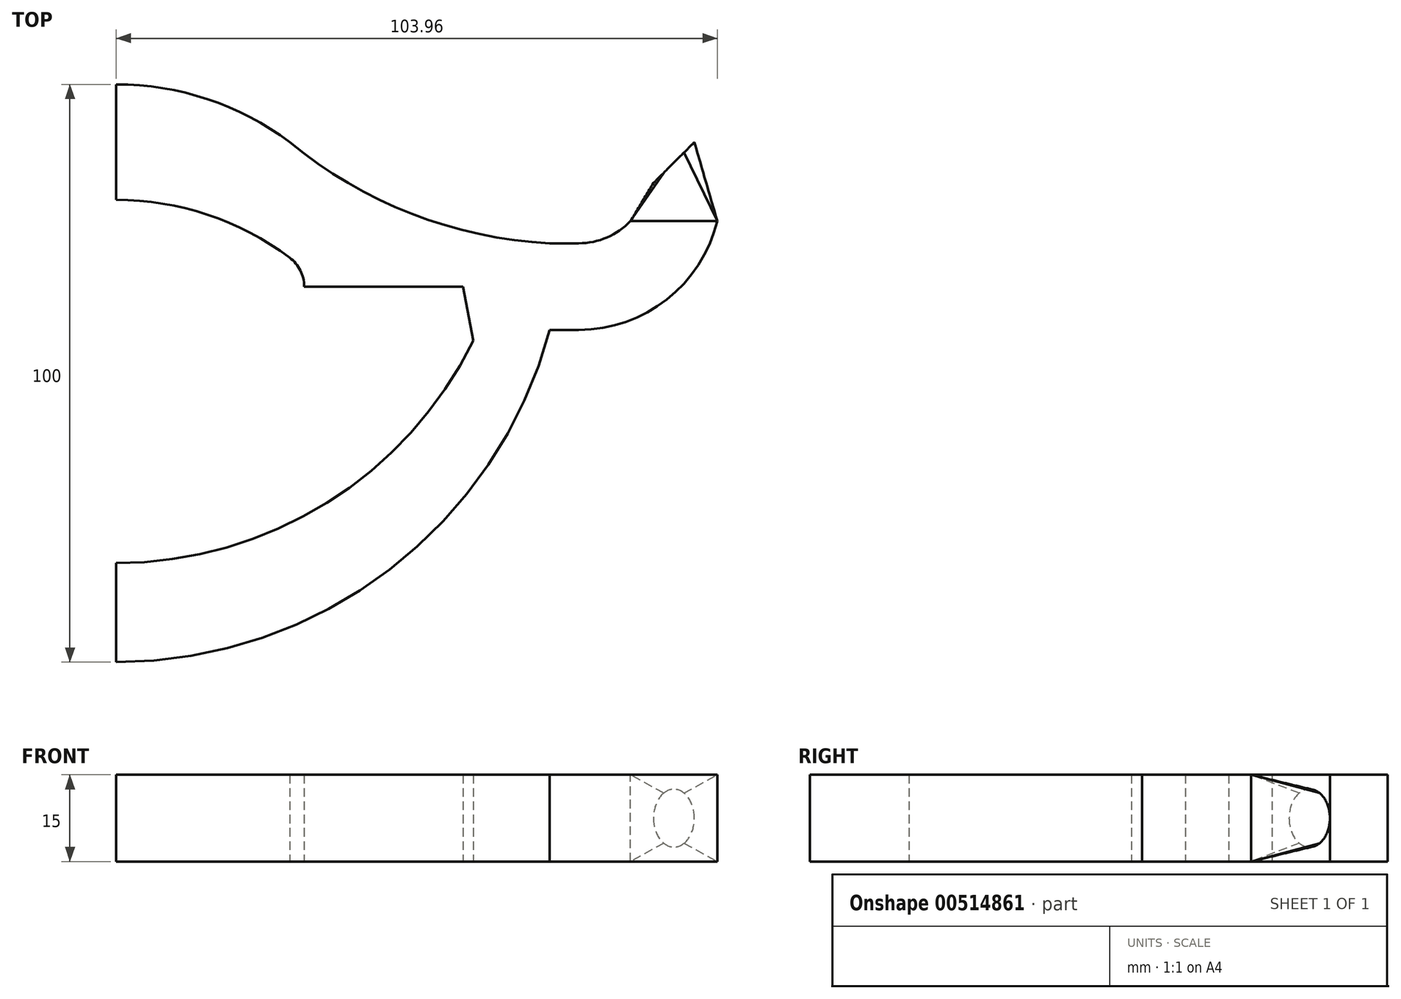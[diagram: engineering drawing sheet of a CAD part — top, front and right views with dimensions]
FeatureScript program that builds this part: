
annotation { "Feature Type Name" : "Feature", "Feature Type Description" : "" }
export const myFeature = defineFeature(function(context is Context, id is Id, definition is map)
    precondition{}
    {
        {
            var Q0;
            Q0=qCreatedBy(makeId("Top.planeOp"),FACE);
            var sketch = newSketch(context, id + "F0", { "sketchPlane" : qUnion([Q0])});
            skLineSegment(sketch, "E0.left", {"start": v(-50, 50) * mm, "end": v(-50, -50) * mm});
            skPoint(sketch, "E0.middle", {"position": v(0, 0) * mm});
            skLineSegment(sketch, "E1", {"start": v(-50, 50) * mm, "end": v(-50, 40) * mm});
            skLineSegment(sketch, "E2", {"start": v(50, 40) * mm, "end": v(42.93, 32.93) * mm});
            skLineSegment(sketch, "E3", {"start": v(42.93, 32.93) * mm, "end": v(46.46, 36.46) * mm});
            skLineSegment(sketch, "E4", {"start": v(-50, 0) * mm, "end": v(-50, -10) * mm});
            skLineSegment(sketch, "E5", {"start": v(-50, -10) * mm, "end": v(-50, 15) * mm});
            skLineSegment(sketch, "E6", {"start": v(-50, 15) * mm, "end": v(114.78, 15) * mm});
            skLineSegment(sketch, "E7", {"start": v(42.93, 32.93) * mm, "end": v(42.93, -37.04) * mm});
            skLineSegment(sketch, "E8", {"start": v(-50, 15) * mm, "end": v(30, 15) * mm});
            skLineSegment(sketch, "E9", {"start": v(30, 15) * mm, "end": v(30, 30) * mm});
            skLineSegment(sketch, "E10", {"start": v(30, 15) * mm, "end": v(30, 0) * mm});
            skLineSegment(sketch, "E11", {"start": v(42.93, 32.93) * mm, "end": v(81, 32.93) * mm});
            skLineSegment(sketch, "E12", {"start": v(46.46, 36.46) * mm, "end": v(46.46, 32.93) * mm});
            skLineSegment(sketch, "E13", {"start": v(46.46, 36.46) * mm, "end": v(46.46, 0) * mm});
            skLineSegment(sketch, "E14", {"start": v(46.46, 36.46) * mm, "end": v(62.14, 20.79) * mm});
            skLineSegment(sketch, "E15", {"start": v(-50, 50) * mm, "end": v(-109.66, 50) * mm});
            skLineSegment(sketch, "E16", {"start": v(-50, 40) * mm, "end": v(-110.5, 40) * mm});
            skLineSegment(sketch, "E17", {"start": v(-50, 15) * mm, "end": v(-113.83, 15) * mm});
            skLineSegment(sketch, "E18", {"start": v(-50, 0) * mm, "end": v(-113, 0) * mm});
            skLineSegment(sketch, "E19", {"start": v(-50, -10) * mm, "end": v(-113, -10) * mm});
            skLineSegment(sketch, "E20", {"start": v(-50, -50) * mm, "end": v(-111.33, -50) * mm});
            skLineSegment(sketch, "E21", {"start": v(30, 30) * mm, "end": v(95.7, 30) * mm});
            skPoint(sketch, "E22", {"position": v(42.93, 30) * mm});
            skPoint(sketch, "E23", {"position": v(46.46, 30) * mm});
            skPoint(sketch, "E24", {"position": v(42.93, 26.34) * mm});
            skLineSegment(sketch, "E25", {"start": v(30, 15) * mm, "end": v(30, 7.5) * mm});
            skLineSegment(sketch, "E26", {"start": v(30, 15) * mm, "end": v(30, 22.5) * mm});
            skLineSegment(sketch, "E27", {"start": v(30, 15) * mm, "end": v(0, 15) * mm});
            skLineSegment(sketch, "E28", {"start": v(-50, 15) * mm, "end": v(-30, 15) * mm});
            skLineSegment(sketch, "E29", {"start": v(-30, 15) * mm, "end": v(-10, 15) * mm});
            skLineSegment(sketch, "E30", {"start": v(-10, 15) * mm, "end": v(10, 15) * mm});
            skSolve(sketch);
        }
        {
            var Q0;
            Q0=sQuery(id+"F0.wireOp",EDGE,"E2");
            cPlane(context, id + "F1", {"entities" : qUnion([Q0]), "cplaneType" : CPlaneType.LINE_ANGLE, "offset" : 25 * mm, "angle" : 90 * degree, "width" : 150 * mm, "height" : 150 * mm});
        }
        {
            var Q0;
            Q0=qCreatedBy(id+"F1.planeOp",FACE);
            var sketch = newSketch(context, id + "F2", { "sketchPlane" : qUnion([Q0])});
            skCircle(sketch, "E31", {"center": v(58.64, 0) * mm, "radius": 5 * mm});
            skSolve(sketch);
        }
        {
            var Q0;
            Q0=sQuery(id+"F0.wireOp",VERTEX,"E6.start");
            var Q1;
            Q1=qCreatedBy(makeId("Right.planeOp"),FACE);
            cPlane(context, id + "F3", {"entities" : qUnion([Q0, Q1]), "cplaneType" : CPlaneType.PLANE_POINT, "offset" : 25 * mm, "width" : 150 * mm, "height" : 150 * mm});
        }
        {
            var Q0;
            Q0=qCreatedBy(id+"F3.planeOp",FACE);
            var sketch = newSketch(context, id + "F4", { "sketchPlane" : qUnion([Q0])});
            skPoint(sketch, "E32", {"position": v(15, 0) * mm});
            skLineSegment(sketch, "E33", {"start": v(50, 10) * mm, "end": v(-20, 10) * mm});
            skLineSegment(sketch, "E34", {"start": v(50, -10) * mm, "end": v(-20, -10) * mm});
            skLineSegment(sketch, "E35", {"start": v(50, 10) * mm, "end": v(50, -10) * mm});
            skLineSegment(sketch, "E36", {"start": v(-20, 10) * mm, "end": v(-20, -10) * mm});
            skLineSegment(sketch, "E37", {"start": v(-49.86, 0) * mm, "end": v(-49.86, 10) * mm});
            skLineSegment(sketch, "E38", {"start": v(-49.86, 0) * mm, "end": v(-49.86, -10) * mm});
            skLineSegment(sketch, "E39", {"start": v(-49.86, 10) * mm, "end": v(-32.86, 10) * mm});
            skLineSegment(sketch, "E40", {"start": v(-32.86, 10) * mm, "end": v(-32.86, -10) * mm});
            skLineSegment(sketch, "E41", {"start": v(-32.86, -10) * mm, "end": v(-49.86, -10) * mm});
            skPoint(sketch, "E42", {"position": v(-32.86, 0) * mm});
            skSolve(sketch);
        }
        {
            var Q0;
            Q0=sQuery(id+"F0.wireOp",VERTEX,"E9.start");
            var Q1;
            Q1=qCreatedBy(id+"F3.planeOp",FACE);
            var Q2;
            Q2=qBodyType(qCreatedBy(id+"FoWz66eWp3AvkS4_1",EDGE),BodyType.WIRE);
            cPlane(context, id + "F5", {"entities" : qUnion([Q0, Q1, Q2]), "cplaneType" : CPlaneType.PLANE_POINT, "offset" : 25 * mm, "width" : 150 * mm, "height" : 150 * mm});
        }
        {
            var Q0;
            Q0=qCreatedBy(id+"F5.planeOp",FACE);
            var sketch = newSketch(context, id + "F6", { "sketchPlane" : qUnion([Q0])});
            skLineSegment(sketch, "E43", {"start": v(22.5, 7.5) * mm, "end": v(7.5, 7.5) * mm});
            skLineSegment(sketch, "E44", {"start": v(22.5, -7.5) * mm, "end": v(7.5, -7.5) * mm});
            skLineSegment(sketch, "E45", {"start": v(22.5, 7.5) * mm, "end": v(22.5, -7.5) * mm});
            skLineSegment(sketch, "E46", {"start": v(7.5, 7.5) * mm, "end": v(7.5, -7.5) * mm});
            skSolve(sketch);
        }
        {
            var Q0;
            Q0=qCreatedBy(makeId("Front.planeOp"),FACE);
            var Q1;
            Q1=sQuery(id+"F0.wireOp",VERTEX,"E24");
            cPlane(context, id + "F7", {"entities" : qUnion([Q0, Q1]), "cplaneType" : CPlaneType.PLANE_POINT, "offset" : 25 * mm, "width" : 150 * mm, "height" : 150 * mm});
        }
        {
            var Q0;
            Q0=qCreatedBy(id+"F7.planeOp",FACE);
            var sketch = newSketch(context, id + "F8", { "sketchPlane" : qUnion([Q0])});
            skPoint(sketch, "E47", {"position": v(46.46, 0) * mm});
            skLineSegment(sketch, "E48", {"start": v(38.96, 0) * mm, "end": v(38.96, -7.5) * mm});
            skLineSegment(sketch, "E49", {"start": v(38.96, 0) * mm, "end": v(38.96, 7.5) * mm});
            skLineSegment(sketch, "E50", {"start": v(53.96, 0) * mm, "end": v(53.96, -7.5) * mm});
            skLineSegment(sketch, "E51", {"start": v(53.96, 0) * mm, "end": v(53.96, 7.5) * mm});
            skLineSegment(sketch, "E52", {"start": v(38.96, -7.5) * mm, "end": v(53.96, -7.5) * mm});
            skLineSegment(sketch, "E53", {"start": v(38.96, 7.5) * mm, "end": v(53.96, 7.5) * mm});
            skSolve(sketch);
        }
        {
            var Q0;
            Q0=makeQuery(id+"F2.imprint","IMPRINT",FACE,{"disambiguationData":[TD([[makeQuery(id+"F2.imprint","IMPRINT",EDGE,{"derivedFrom":sQuery(id+"F2.wireOp",EDGE,"E31")}),1.0]])]});
            var Q1;
            Q1=makeQuery(id+"F8.imprint","IMPRINT",FACE,{"disambiguationData":[TD([[makeQuery(id+"F8.imprint","IMPRINT",EDGE,{"derivedFrom":sQuery(id+"F8.wireOp",EDGE,"E48")}),1.0]])]});
            loft(context, id + "F9", {"sheetProfilesArray" : [{ "sheetProfileEntities" : qUnion([Q0]) }, { "sheetProfileEntities" : qUnion([Q1]) }]});
        }
        {
            var Q0;
            Q0=sQuery(id+"F0.wireOp",VERTEX,"E17.start");
            var Q1;
            Q1=qCreatedBy(makeId("Right.planeOp"),FACE);
            cPlane(context, id + "F10", {"entities" : qUnion([Q0, Q1]), "cplaneType" : CPlaneType.PLANE_POINT, "offset" : 25 * mm, "width" : 150 * mm, "height" : 150 * mm});
        }
        {
            var Q0;
            Q0=sQuery(id+"F0.wireOp",VERTEX,"E30.end");
            var Q1;
            Q1=qCreatedBy(id+"F5.planeOp",FACE);
            cPlane(context, id + "F11", {"entities" : qUnion([Q0, Q1]), "cplaneType" : CPlaneType.PLANE_POINT, "offset" : 25 * mm, "width" : 150 * mm, "height" : 150 * mm});
        }
        {
            var Q0;
            Q0=qCreatedBy(id+"F11.planeOp",FACE);
            var sketch = newSketch(context, id + "F12", { "sketchPlane" : qUnion([Q0])});
            skPoint(sketch, "E54", {"position": v(15, 0) * mm});
            skLineSegment(sketch, "E55", {"start": v(30, -10) * mm, "end": v(30, 10) * mm});
            skLineSegment(sketch, "E56", {"start": v(0, 10) * mm, "end": v(0, -10) * mm});
            skLineSegment(sketch, "E57", {"start": v(30, 10) * mm, "end": v(0, 10) * mm});
            skLineSegment(sketch, "E58", {"start": v(30, -10) * mm, "end": v(0, -10) * mm});
            skSolve(sketch);
        }
        {
            var Q0;
            Q0=sQuery(id+"F0.wireOp",VERTEX,"E30.start");
            var Q1;
            Q1=qCreatedBy(makeId("Right.planeOp"),FACE);
            cPlane(context, id + "F13", {"entities" : qUnion([Q0, Q1]), "cplaneType" : CPlaneType.PLANE_POINT, "offset" : 25 * mm, "width" : 150 * mm, "height" : 150 * mm});
        }
        {
            var Q0;
            Q0=sQuery(id+"F0.wireOp",VERTEX,"E29.start");
            var Q1;
            Q1=qCreatedBy(id+"F13.planeOp",FACE);
            cPlane(context, id + "F14", {"entities" : qUnion([Q0, Q1]), "cplaneType" : CPlaneType.PLANE_POINT, "offset" : 25 * mm, "width" : 150 * mm, "height" : 150 * mm});
        }
        {
            var Q0;
            Q0=sQuery(id+"F8.wireOp",VERTEX,"E48.start");
            var Q1;
            Q1=qCreatedBy(makeId("Top.planeOp"),FACE);
            cPlane(context, id + "F15", {"entities" : qUnion([Q0, Q1]), "cplaneType" : CPlaneType.PLANE_POINT, "offset" : 25 * mm, "width" : 150 * mm, "height" : 150 * mm});
        }
        {
            var Q0;
            Q0=qCreatedBy(id+"F15.planeOp",FACE);
            var sketch = newSketch(context, id + "F16", { "sketchPlane" : qUnion([Q0])});
            skPoint(sketch, "E59", {"position": v(30, 22.5) * mm});
            skPoint(sketch, "E60", {"position": v(38.96, 26.34) * mm});
            skPoint(sketch, "E61", {"position": v(30, 7.5) * mm});
            skPoint(sketch, "E62", {"position": v(53.96, 26.34) * mm});
            skArc(sketch, "E63", {"start": v(30, 22.5) * mm, "mid": v(34.88, 23.5) * mm, "end": v(38.96, 26.34) * mm});
            skArc(sketch, "E64", {"start": v(30, 7.5) * mm, "mid": v(45.24, 12.77) * mm, "end": v(53.96, 26.34) * mm});
            skLineSegment(sketch, "E65", {"start": v(30, 22.5) * mm, "end": v(30, 7.5) * mm});
            skLineSegment(sketch, "E66", {"start": v(38.96, 26.34) * mm, "end": v(53.96, 26.34) * mm});
            skSolve(sketch);
        }
        {
            var Q0;
            Q0=makeQuery(id+"F16.imprint","IMPRINT",FACE,{"disambiguationData":[TD([[makeQuery(id+"F16.imprint","IMPRINT",EDGE,{"derivedFrom":sQuery(id+"F16.wireOp",EDGE,"E63")}),-1.0]])]});
            extrude(context, id + "F17", {"entities" : qUnion([Q0]), "operationType" : NewBodyOperationType.ADD, "endBound" : BoundingType.SYMMETRIC, "depth" : 15 * mm, "offsetDistance" : 25 * mm});
        }
        {
            var Q0;
            Q0=qCreatedBy(makeId("Top.planeOp"),FACE);
            var sketch = newSketch(context, id + "F18", { "sketchPlane" : qUnion([Q0])});
            skPoint(sketch, "E67", {"position": v(30, 22.5) * mm});
            skPoint(sketch, "E68", {"position": v(30, 7.5) * mm});
            skPoint(sketch, "E69", {"position": v(-50, 50) * mm});
            skPoint(sketch, "E70", {"position": v(-50, -20) * mm});
            skLineSegment(sketch, "E71", {"start": v(-50, 50) * mm, "end": v(-56.58, 50) * mm});
            skLineSegment(sketch, "E72", {"start": v(-50, -20) * mm, "end": v(-57.7, -20) * mm});
            skLineSegment(sketch, "E73", {"start": v(30, 22.5) * mm, "end": v(25, 22.5) * mm});
            skPoint(sketch, "E74", {"position": v(-50, 40) * mm});
            skPoint(sketch, "E75", {"position": v(-50, 15) * mm});
            skPoint(sketch, "E76", {"position": v(-50, 0) * mm});
            skPoint(sketch, "E77", {"position": v(-50, -10) * mm});
            skLineSegment(sketch, "E78.MirrorCS", {"start": v(30, 7.5) * mm, "end": v(25, 7.5) * mm});
            skLineSegment(sketch, "E79", {"start": v(-50, 50) * mm, "end": v(-50, -20) * mm});
            skLineSegment(sketch, "E80", {"start": v(30, 22.5) * mm, "end": v(30, 7.5) * mm});
            skLineSegment(sketch, "E81", {"start": v(25, 22.5) * mm, "end": v(25, 7.5) * mm});
            skPoint(sketch, "E82", {"position": v(25, 15) * mm});
            skLineSegment(sketch, "E83", {"start": v(25, 15) * mm, "end": v(-20, 15) * mm});
            skLineSegment(sketch, "E84", {"start": v(-50, 40) * mm, "end": v(-20, 40) * mm});
            skArc(sketch, "E85", {"start": v(-20, 40) * mm, "mid": v(-34.19, 47.43) * mm, "end": v(-50, 50) * mm});
            skLineSegment(sketch, "E86", {"start": v(-20, 40) * mm, "end": v(-14.1, 35.57) * mm});
            skArc(sketch, "E87", {"start": v(-20, 40) * mm, "mid": v(1.08, 27.6) * mm, "end": v(25, 22.5) * mm});
            skArc(sketch, "E88.MirrorCS", {"start": v(-20, -10) * mm, "mid": v(-34.19, -17.43) * mm, "end": v(-50, -20) * mm});
            skArc(sketch, "E89.MirrorCS", {"start": v(-20, -10) * mm, "mid": v(1.08, 2.4) * mm, "end": v(25, 7.5) * mm});
            skPoint(sketch, "E90", {"position": v(10, 15) * mm});
            skLineSegment(sketch, "E91", {"start": v(11.77, 5.67) * mm, "end": v(10, 15) * mm});
            skPoint(sketch, "E92", {"position": v(-50, -32.86) * mm});
            skPoint(sketch, "E93", {"position": v(-50, -50) * mm});
            skLineSegment(sketch, "E94", {"start": v(-50, -32.86) * mm, "end": v(-55.92, -32.86) * mm});
            skLineSegment(sketch, "E95", {"start": v(-50, -32.86) * mm, "end": v(-50, -42.86) * mm});
            skLineSegment(sketch, "E96", {"start": v(-50, -42.86) * mm, "end": v(-32.06, -42.86) * mm});
            skLineSegment(sketch, "E97", {"start": v(-50, -20) * mm, "end": v(-50, -24.93) * mm});
            skLineSegment(sketch, "E98", {"start": v(-50, -24.93) * mm, "end": v(-42.8, -24.93) * mm});
            skLineSegment(sketch, "E99", {"start": v(-50, -32.86) * mm, "end": v(-5.32, -32.86) * mm});
            skLineSegment(sketch, "E100", {"start": v(-20, -10) * mm, "end": v(-18.9, -9.1) * mm});
            skLineSegment(sketch, "E101", {"start": v(-50, -50) * mm, "end": v(-61.6, -50) * mm});
            skLineSegment(sketch, "E102", {"start": v(-20, -37.52) * mm, "end": v(-20, -61.03) * mm});
            skLineSegment(sketch, "E103", {"start": v(-50, -50) * mm, "end": v(-20, -50) * mm});
            skArc(sketch, "E104", {"start": v(-50, -32.86) * mm, "mid": v(-13.6, -22.43) * mm, "end": v(11.77, 5.67) * mm});
            skArc(sketch, "E105", {"start": v(-50, -50) * mm, "mid": v(-2.75, -33.97) * mm, "end": v(25, 7.5) * mm});
            skLineSegment(sketch, "E106", {"start": v(-50, -32.86) * mm, "end": v(-50, -50) * mm});
            skLineSegment(sketch, "E107", {"start": v(-50, 15) * mm, "end": v(-50, 24) * mm});
            skLineSegment(sketch, "E108", {"start": v(-50, 15) * mm, "end": v(-50, 6) * mm});
            skLineSegment(sketch, "E109", {"start": v(-50, -20) * mm, "end": v(-50, 5) * mm});
            skLineSegment(sketch, "E110", {"start": v(-50, 5) * mm, "end": v(-40.99, 5) * mm});
            skArc(sketch, "E111.MirrorCS", {"start": v(-20, 20) * mm, "mid": v(-34.19, 27.43) * mm, "end": v(-50, 30) * mm});
            skLineSegment(sketch, "E112", {"start": v(-50, 50) * mm, "end": v(-50, 25) * mm});
            skLineSegment(sketch, "E113", {"start": v(-50, 25) * mm, "end": v(-38.68, 25) * mm});
            skArc(sketch, "E114.MirrorCS", {"start": v(-20, 10) * mm, "mid": v(-34.19, 2.57) * mm, "end": v(-50, 0) * mm});
            skLineSegment(sketch, "E115", {"start": v(-20, 20) * mm, "end": v(-20, 10) * mm});
            skLineSegment(sketch, "E116", {"start": v(-20, 10) * mm, "end": v(-15.23, 13.58) * mm});
            skLineSegment(sketch, "E117", {"start": v(-20, 20) * mm, "end": v(-16.17, 17.13) * mm});
            skArc(sketch, "E118", {"start": v(-20, 10) * mm, "mid": v(-17.5, 15) * mm, "end": v(-20, 20) * mm});
            skSolve(sketch);
        }
        {
            var Q0;
            Q0=makeQuery(id+"F18.imprint","IMPRINT",FACE,{"disambiguationData":[TD([[makeQuery(id+"F18.imprint","IMPRINT",EDGE,{"derivedFrom":sQuery(id+"F18.wireOp",EDGE,"E73")}),1.0]])]});
            extrude(context, id + "F19", {"entities" : qUnion([Q0]), "operationType" : NewBodyOperationType.ADD, "endBound" : BoundingType.SYMMETRIC, "depth" : 15 * mm, "offsetDistance" : 25 * mm});
        }
        {
            var Q0;
            {var subQ2=sQuery(id+"F18.wireOp",EDGE,"E84");Q0=makeQuery(id+"F18.imprint","IMPRINT",FACE,{"disambiguationData":[TD([[makeQuery(id+"F18.imprint","IMPRINT",EDGE,{"derivedFrom":subQ2}),1.0]])]});}
            var Q1;
            {var subQ0=sQuery(id+"F18.wireOp",EDGE,"E84");Q1=makeQuery(id+"F18.imprint","IMPRINT",FACE,{"disambiguationData":[TD([[makeQuery(id+"F18.imprint","IMPRINT",EDGE,{"derivedFrom":subQ0}),-1.0]])]});}
            var Q2;
            {var subQ6=sQuery(id+"F18.wireOp",EDGE,"E104");Q2=makeQuery(id+"F18.imprint","IMPRINT",FACE,{"disambiguationData":[TD([[makeQuery(id+"F18.imprint","IMPRINT",EDGE,{"derivedFrom":subQ6}),-1.0]])]});}
            var Q3;
            {var subQ5=sQuery(id+"F18.wireOp",EDGE,"E91");Q3=makeQuery(id+"F18.imprint","IMPRINT",FACE,{"disambiguationData":[TD([[makeQuery(id+"F18.imprint","IMPRINT",EDGE,{"derivedFrom":subQ5}),-1.0]])]});}
            var Q4;
            {var subQ4=sQuery(id+"F18.wireOp",EDGE,"E88.MirrorCS");Q4=makeQuery(id+"F18.imprint","IMPRINT",FACE,{"disambiguationData":[TD([[makeQuery(id+"F18.imprint","IMPRINT",EDGE,{"derivedFrom":subQ4}),-1.0]])]});}
            extrude(context, id + "F20", {"entities" : qUnion([Q0, Q1, Q2, Q3, Q4]), "operationType" : NewBodyOperationType.ADD, "endBound" : BoundingType.SYMMETRIC, "depth" : 15 * mm, "offsetDistance" : 25 * mm});
        }
    });
